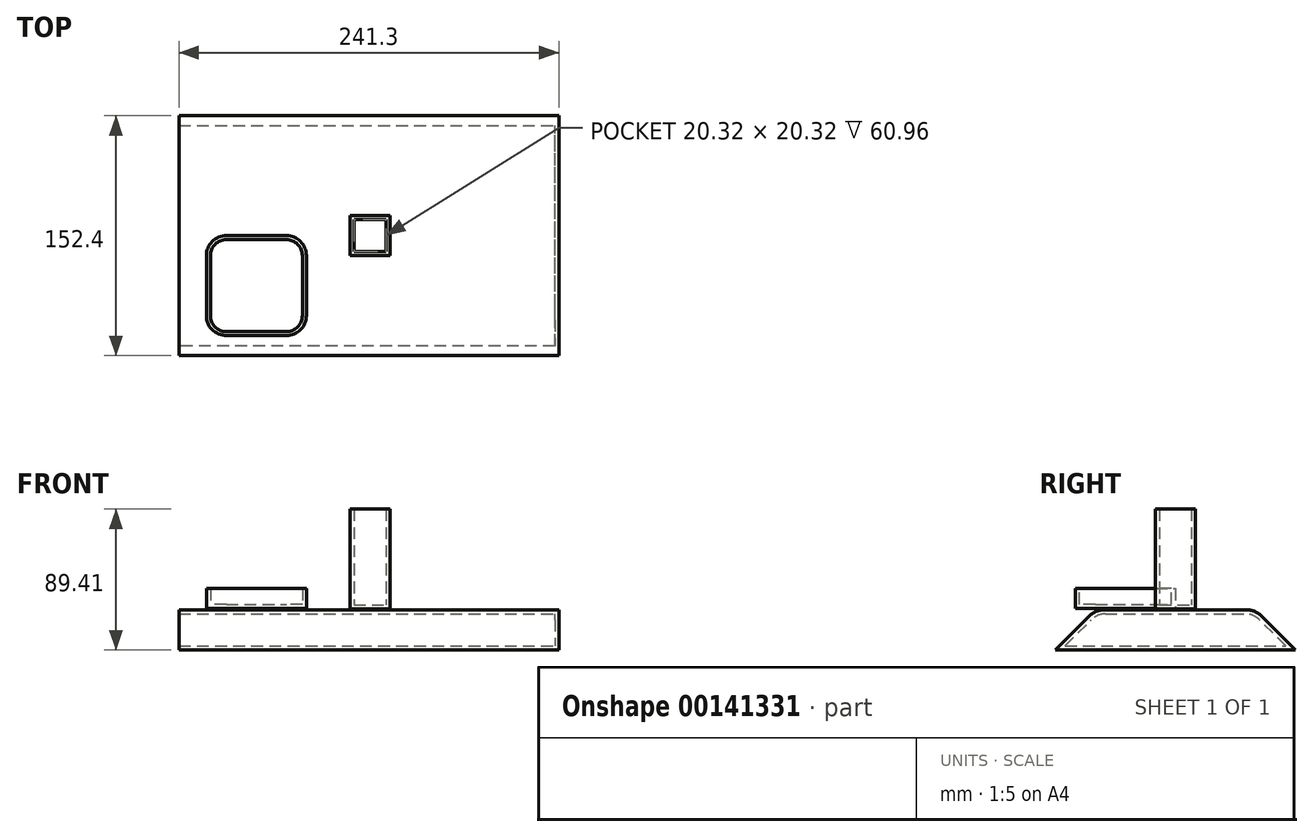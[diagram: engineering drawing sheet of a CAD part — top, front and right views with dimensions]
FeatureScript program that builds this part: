
annotation { "Feature Type Name" : "Feature", "Feature Type Description" : "" }
export const myFeature = defineFeature(function(context is Context, id is Id, definition is map)
    precondition{}
    {
        {
            var Q0;
            Q0=qCreatedBy(makeId("Front.planeOp"),FACE);
            var sketch = newSketch(context, id + "F0", { "sketchPlane" : qUnion([Q0])});
            skLineSegment(sketch, "E0.bottom", {"start": v(0, -73.69) * mm, "end": v(-241.3, -73.69) * mm});
            skLineSegment(sketch, "E0.top", {"start": v(0, -48.29) * mm, "end": v(-241.3, -48.29) * mm});
            skLineSegment(sketch, "E0.left", {"start": v(0, -73.69) * mm, "end": v(0, -48.29) * mm});
            skLineSegment(sketch, "E0.right", {"start": v(-241.3, -73.69) * mm, "end": v(-241.3, -48.29) * mm});
            skPoint(sketch, "E0.middle", {"position": v(-120.65, -60.99) * mm});
            skLineSegment(sketch, "E1", {"start": v(-36.23, -48.29) * mm, "end": v(-36.23, 91.41) * mm});
            skLineSegment(sketch, "E2", {"start": v(-57.88, -48.29) * mm, "end": v(-57.88, 78.71) * mm});
            skLineSegment(sketch, "E3", {"start": v(-79.53, -48.29) * mm, "end": v(-79.53, 66.01) * mm});
            skLineSegment(sketch, "E4.bottom", {"start": v(-132.55, -48.29) * mm, "end": v(-107.15, -48.29) * mm});
            skLineSegment(sketch, "E4.top", {"start": v(-132.55, 15.21) * mm, "end": v(-107.15, 15.21) * mm});
            skLineSegment(sketch, "E4.left", {"start": v(-132.55, -48.29) * mm, "end": v(-132.55, 15.21) * mm});
            skLineSegment(sketch, "E4.right", {"start": v(-107.15, -48.29) * mm, "end": v(-107.15, 15.21) * mm});
            skLineSegment(sketch, "E5.bottom", {"start": v(-223.13, -48.29) * mm, "end": v(-159.63, -48.29) * mm});
            skLineSegment(sketch, "E5.top", {"start": v(-223.13, -35.59) * mm, "end": v(-159.63, -35.59) * mm});
            skLineSegment(sketch, "E5.left", {"start": v(-223.13, -48.29) * mm, "end": v(-223.13, -35.59) * mm});
            skLineSegment(sketch, "E5.right", {"start": v(-159.63, -48.29) * mm, "end": v(-159.63, -35.59) * mm});
            skSolve(sketch);
        }
        {
            var Q0;
            Q0=makeQuery(id+"F0.imprint","IMPRINT",FACE,{"disambiguationData":[TD([[makeQuery(id+"F0.imprint","IMPRINT",EDGE,{"derivedFrom":sQuery(id+"F0.wireOp",EDGE,"E0.bottom")}),-1.0]])]});
            extrude(context, id + "F1", {"entities" : qUnion([Q0]), "endBound" : BoundingType.SYMMETRIC, "depth" : 152.4 * mm});
        }
        {
            var Q0;
            Q0=qCreatedBy(makeId("Front.planeOp"),FACE);
            var sketch = newSketch(context, id + "F2", { "sketchPlane" : qUnion([Q0])});
            skLineSegment(sketch, "E6.bottom", {"start": v(-132.7, 15.72) * mm, "end": v(-107.3, 15.72) * mm});
            skLineSegment(sketch, "E6.top", {"start": v(-132.7, -47.78) * mm, "end": v(-107.3, -47.78) * mm});
            skLineSegment(sketch, "E6.left", {"start": v(-132.7, 15.72) * mm, "end": v(-132.7, -47.78) * mm});
            skLineSegment(sketch, "E6.right", {"start": v(-107.3, 15.72) * mm, "end": v(-107.3, -47.78) * mm});
            skSolve(sketch);
        }
        {
            var Q0;
            Q0=makeQuery(id+"F2.imprint","IMPRINT",FACE,{"disambiguationData":[TD([[makeQuery(id+"F2.imprint","IMPRINT",EDGE,{"derivedFrom":sQuery(id+"F2.wireOp",EDGE,"E6.bottom")}),-1.0]])]});
            extrude(context, id + "F3", {"entities" : qUnion([Q0]), "endBound" : BoundingType.SYMMETRIC, "depth" : 25.4 * mm});
        }
        {
            var Q0;
            Q0=qCreatedBy(makeId("Front.planeOp"),FACE);
            var sketch = newSketch(context, id + "F4", { "sketchPlane" : qUnion([Q0])});
            skLineSegment(sketch, "E7.bottom", {"start": v(-223.81, -34.67) * mm, "end": v(-160.31, -34.67) * mm});
            skLineSegment(sketch, "E7.top", {"start": v(-223.81, -47.37) * mm, "end": v(-160.31, -47.37) * mm});
            skLineSegment(sketch, "E7.left", {"start": v(-223.81, -34.67) * mm, "end": v(-223.81, -47.37) * mm});
            skLineSegment(sketch, "E7.right", {"start": v(-160.31, -34.67) * mm, "end": v(-160.31, -47.37) * mm});
            skSolve(sketch);
        }
        {
            var Q0;
            Q0 = qSketchRegion(id + "F4", true);
            extrude(context, id + "F5", {"entities" : qUnion([Q0]), "depth" : 63.5 * mm});
        }
        {
            var Q0;
            Q0=makeQuery(id+"F1.opExtrude","SWEPT_FACE",FACE,{"disambiguationData":[OSD([sQuery(id+"F0.wireOp",EDGE,"E0.right")])]});
            var sketch = newSketch(context, id + "F6", { "sketchPlane" : qUnion([Q0])});
            skSolve(sketch);
        }
        {
            var Q0;
            Q0=makeQuery(id+"F1.opExtrude","CAP_EDGE",EDGE,{"disambiguationData":[OSD([sQuery(id+"F0.wireOp",EDGE,"E0.top"),sQuery(id+"F0.wireOp",EDGE,"E4.bottom"),sQuery(id+"F0.wireOp",EDGE,"E5.bottom")])],"isStart":false});
            chamfer(context, id + "F7", {"entities" : qUnion([Q0]), "width" : 25.4 * mm, "tangentPropagation" : true});
        }
        {
            var Q0;
            Q0=makeQuery(id+"F1.opExtrude","CAP_EDGE",EDGE,{"disambiguationData":[OSD([sQuery(id+"F0.wireOp",EDGE,"E0.top"),sQuery(id+"F0.wireOp",EDGE,"E4.bottom"),sQuery(id+"F0.wireOp",EDGE,"E5.bottom")])],"isStart":true});
            chamfer(context, id + "F8", {"entities" : qUnion([Q0]), "width" : 25.4 * mm, "tangentPropagation" : true});
        }
        {
            var Q0;
            Q0=makeQuery(id+"F1.opExtrude","SWEPT_FACE",FACE,{"disambiguationData":[OSD([sQuery(id+"F0.wireOp",EDGE,"E0.right")])]});
            shell(context, id + "F9", {"entities" : qUnion([Q0]), "thickness" : 2.54 * mm});
        }
        {
            var Q0;
            Q0=makeQuery(id+"F3.opExtrude","SWEPT_FACE",FACE,{"disambiguationData":[OSD([sQuery(id+"F2.wireOp",EDGE,"E6.bottom")])]});
            shell(context, id + "F10", {"entities" : qUnion([Q0]), "thickness" : 2.54 * mm});
        }
        {
            var Q0;
            Q0=makeQuery(id+"F5.opExtrude","CAP_EDGE",EDGE,{"disambiguationData":[OSD([sQuery(id+"F4.wireOp",EDGE,"E7.left")])],"isStart":false});
            var Q1;
            Q1=makeQuery(id+"F5.opExtrude","CAP_EDGE",EDGE,{"disambiguationData":[OSD([sQuery(id+"F4.wireOp",EDGE,"E7.left")])],"isStart":true});
            var Q2;
            Q2=makeQuery(id+"F5.opExtrude","CAP_EDGE",EDGE,{"disambiguationData":[OSD([sQuery(id+"F4.wireOp",EDGE,"E7.right")])],"isStart":true});
            var Q3;
            Q3=makeQuery(id+"F5.opExtrude","CAP_EDGE",EDGE,{"disambiguationData":[OSD([sQuery(id+"F0.wireOp",EDGE,"E5.right")])],"isStart":false});
            fillet(context, id + "F11", {"entities" : qUnion([Q0, Q1, Q2, Q3]), "radius" : 12.7 * mm, "tangentPropagation" : true, "allowEdgeOverflow" : false});
        }
        {
            var Q0;
            Q0=makeQuery(id+"F5.opExtrude","CAP_EDGE",EDGE,{"disambiguationData":[OSD([sQuery(id+"F4.wireOp",EDGE,"E7.right")])],"isStart":false});
            fillet(context, id + "F12", {"entities" : qUnion([Q0]), "radius" : 12.7 * mm, "tangentPropagation" : true, "allowEdgeOverflow" : false});
        }
        {
            var Q0;
            {var subQ0=sQuery(id+"F0.wireOp",EDGE,"E5.bottom");var subQ1=sQuery(id+"F0.wireOp",EDGE,"E4.bottom");var subQ2=sQuery(id+"F0.wireOp",EDGE,"E0.top");Q0=makeQuery(id+"F7.opChamfer","BLEND_EDGE",EDGE,{"blendedFrom":[makeQuery(id+"F1.opExtrude","CAP_EDGE",EDGE,{"disambiguationData":[OSD([subQ2,subQ1,subQ0])],"isStart":false}),makeQuery(id+"F1.opExtrude","SWEPT_FACE",FACE,{"disambiguationData":[OSD([subQ2,subQ1,subQ0])]})],"blendedInto":[makeQuery(id+"F1.opExtrude","SWEPT_FACE",FACE,{"disambiguationData":[OSD([subQ2,subQ1,subQ0])]})]});}
            var Q1;
            {var subQ0=sQuery(id+"F0.wireOp",EDGE,"E5.bottom");var subQ1=sQuery(id+"F0.wireOp",EDGE,"E4.bottom");var subQ2=sQuery(id+"F0.wireOp",EDGE,"E0.top");Q1=makeQuery(id+"F8.opChamfer","BLEND_EDGE",EDGE,{"blendedFrom":[makeQuery(id+"F1.opExtrude","CAP_EDGE",EDGE,{"disambiguationData":[OSD([subQ2,subQ1,subQ0])],"isStart":true}),makeQuery(id+"F1.opExtrude","SWEPT_FACE",FACE,{"disambiguationData":[OSD([subQ2,subQ1,subQ0])]})],"blendedInto":[makeQuery(id+"F1.opExtrude","SWEPT_FACE",FACE,{"disambiguationData":[OSD([subQ2,subQ1,subQ0])]})]});}
            fillet(context, id + "F13", {"entities" : qUnion([Q0, Q1]), "radius" : 12.7 * mm, "tangentPropagation" : true, "allowEdgeOverflow" : false});
        }
        {
            var Q0;
            {var subQ0=sQuery(id+"F0.wireOp",EDGE,"E5.bottom");var subQ1=sQuery(id+"F0.wireOp",EDGE,"E4.bottom");var subQ2=sQuery(id+"F0.wireOp",EDGE,"E0.top");Q0=makeQuery(id+"F9.opShell","OFFSET_EDGE",EDGE,{"disambiguationData":[OSD([subQ2,subQ1,subQ0]),TDD([makeQuery(id+"F8.opChamfer","BLEND_EDGE",EDGE,{"blendedFrom":[makeQuery(id+"F1.opExtrude","CAP_EDGE",EDGE,{"disambiguationData":[OSD([subQ2,subQ1,subQ0])],"isStart":true}),makeQuery(id+"F1.opExtrude","SWEPT_FACE",FACE,{"disambiguationData":[OSD([subQ2,subQ1,subQ0])]})],"blendedInto":[makeQuery(id+"F1.opExtrude","SWEPT_FACE",FACE,{"disambiguationData":[OSD([subQ2,subQ1,subQ0])]})]})])]});}
            var Q1;
            {var subQ0=sQuery(id+"F0.wireOp",EDGE,"E5.bottom");var subQ1=sQuery(id+"F0.wireOp",EDGE,"E4.bottom");var subQ2=sQuery(id+"F0.wireOp",EDGE,"E0.top");Q1=makeQuery(id+"F9.opShell","OFFSET_EDGE",EDGE,{"disambiguationData":[OSD([subQ2,subQ1,subQ0]),TDD([makeQuery(id+"F7.opChamfer","BLEND_EDGE",EDGE,{"blendedFrom":[makeQuery(id+"F1.opExtrude","CAP_EDGE",EDGE,{"disambiguationData":[OSD([subQ2,subQ1,subQ0])],"isStart":false}),makeQuery(id+"F1.opExtrude","SWEPT_FACE",FACE,{"disambiguationData":[OSD([subQ2,subQ1,subQ0])]})],"blendedInto":[makeQuery(id+"F1.opExtrude","SWEPT_FACE",FACE,{"disambiguationData":[OSD([subQ2,subQ1,subQ0])]})]})])]});}
            fillet(context, id + "F14", {"entities" : qUnion([Q0, Q1]), "radius" : 12.7 * mm, "tangentPropagation" : true, "allowEdgeOverflow" : false});
        }
        {
            var Q0;
            Q0=makeQuery(id+"F5.opExtrude","SWEPT_FACE",FACE,{"disambiguationData":[OSD([sQuery(id+"F4.wireOp",EDGE,"E7.bottom")])]});
            shell(context, id + "F15", {"entities" : qUnion([Q0]), "thickness" : 2.54 * mm});
        }
    });
